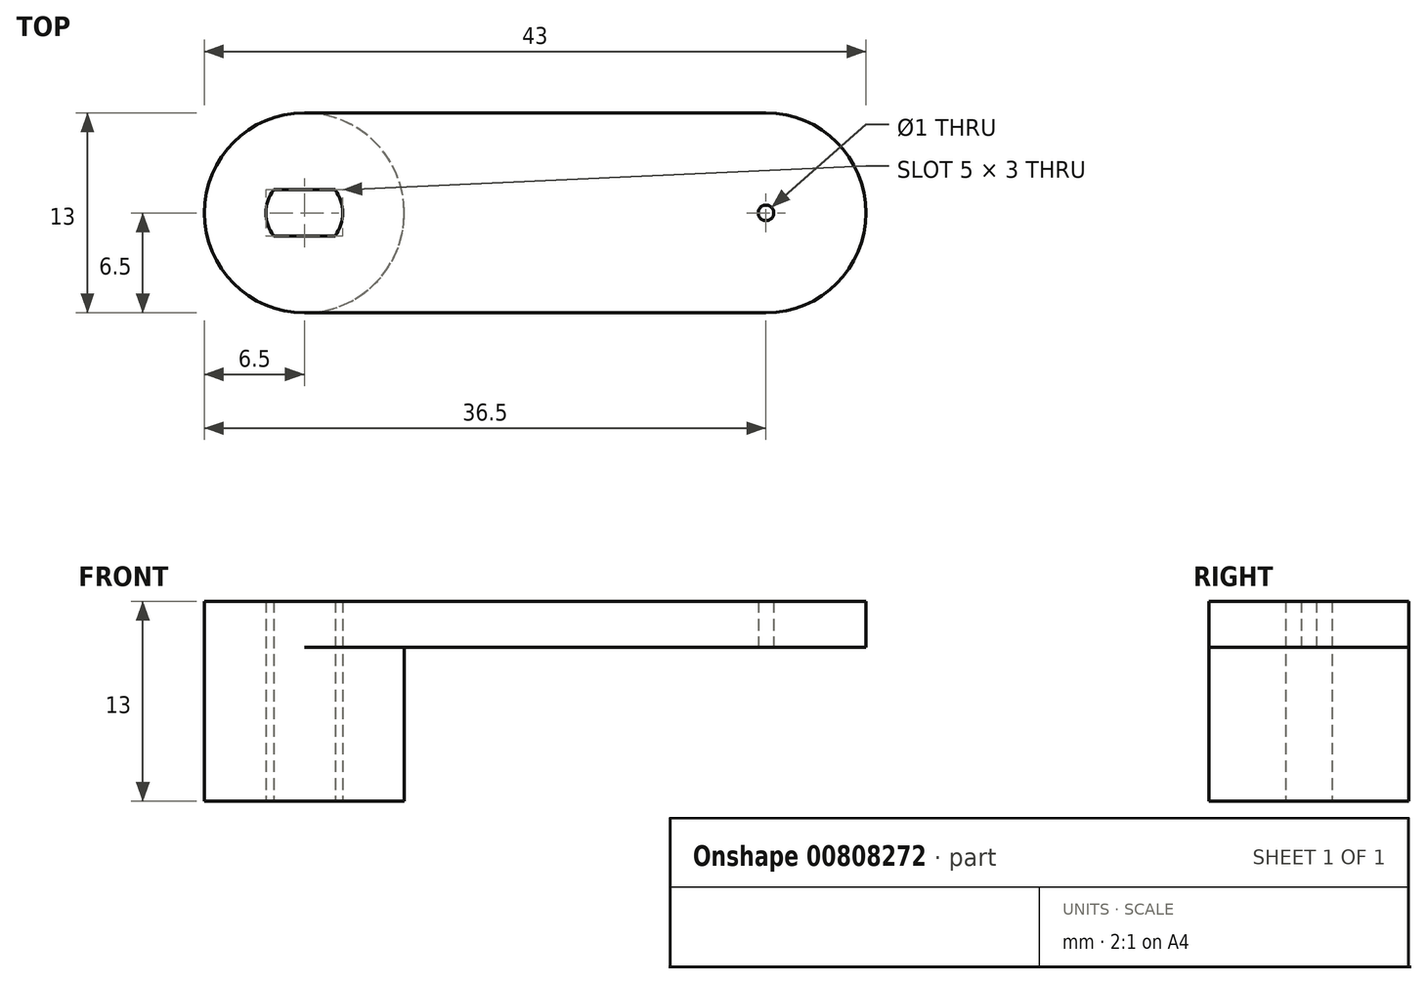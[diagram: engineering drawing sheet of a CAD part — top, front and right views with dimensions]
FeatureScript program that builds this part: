
annotation { "Feature Type Name" : "Feature", "Feature Type Description" : "" }
export const myFeature = defineFeature(function(context is Context, id is Id, definition is map)
    precondition{}
    {
        {
            var Q0;
            Q0=qCreatedBy(makeId("Top.planeOp"),FACE);
            var sketch = newSketch(context, id + "F0", { "sketchPlane" : qUnion([Q0])});
            skCircle(sketch, "E0", {"center": v(0, 0) * mm, "radius": 6.5 * mm});
            skArc(sketch, "E1", {"start": v(2, -1.5) * mm, "mid": v(2.5, 0) * mm, "end": v(2, 1.5) * mm});
            skLineSegment(sketch, "E2", {"start": v(-2, 1.5) * mm, "end": v(2, 1.5) * mm});
            skLineSegment(sketch, "E3", {"start": v(2, -1.5) * mm, "end": v(-2, -1.5) * mm});
            skLineSegment(sketch, "E4", {"start": v(0, 6.5) * mm, "end": v(30, 6.5) * mm});
            skLineSegment(sketch, "E5", {"start": v(0, -6.5) * mm, "end": v(30, -6.5) * mm});
            skCircle(sketch, "E6", {"center": v(30, 0) * mm, "radius": 6.5 * mm});
            skCircle(sketch, "E7", {"center": v(30, 0) * mm, "radius": 0.5 * mm});
            skArc(sketch, "E8.trimOffspring", {"start": v(-2, 1.5) * mm, "mid": v(-2.5, 0) * mm, "end": v(-2, -1.5) * mm});
            skSolve(sketch);
        }
        {
            var Q0;
            Q0=makeQuery(id+"F0.imprint","IMPRINT",FACE,{"disambiguationData":[TD([[makeQuery(id+"F0.imprint","IMPRINT",EDGE,{"derivedFrom":sQuery(id+"F0.wireOp",EDGE,"E1")}),-1.0]])]});
            var Q1;
            {var subQ0=sQuery(id+"F0.wireOp",EDGE,"E4");Q1=makeQuery(id+"F0.imprint","IMPRINT",FACE,{"disambiguationData":[TD([[makeQuery(id+"F0.imprint","IMPRINT",EDGE,{"derivedFrom":subQ0}),-1.0]])]});}
            var Q2;
            Q2=makeQuery(id+"F0.imprint","IMPRINT",FACE,{"disambiguationData":[TD([[makeQuery(id+"F0.imprint","IMPRINT",EDGE,{"derivedFrom":sQuery(id+"F0.wireOp",EDGE,"E7")}),-1.0]])]});
            extrude(context, id + "F1", {"entities" : qUnion([Q0, Q1, Q2]), "depth" : 3 * mm, "offsetDistance" : 25 * mm});
        }
        {
            var Q0;
            Q0=makeQuery(id+"F0.imprint","IMPRINT",FACE,{"disambiguationData":[TD([[makeQuery(id+"F0.imprint","IMPRINT",EDGE,{"derivedFrom":sQuery(id+"F0.wireOp",EDGE,"E1")}),-1.0]])]});
            extrude(context, id + "F2", {"entities" : qUnion([Q0]), "operationType" : NewBodyOperationType.ADD, "oppositeDirection" : true, "depth" : 10 * mm, "offsetDistance" : 25 * mm});
        }
    });
